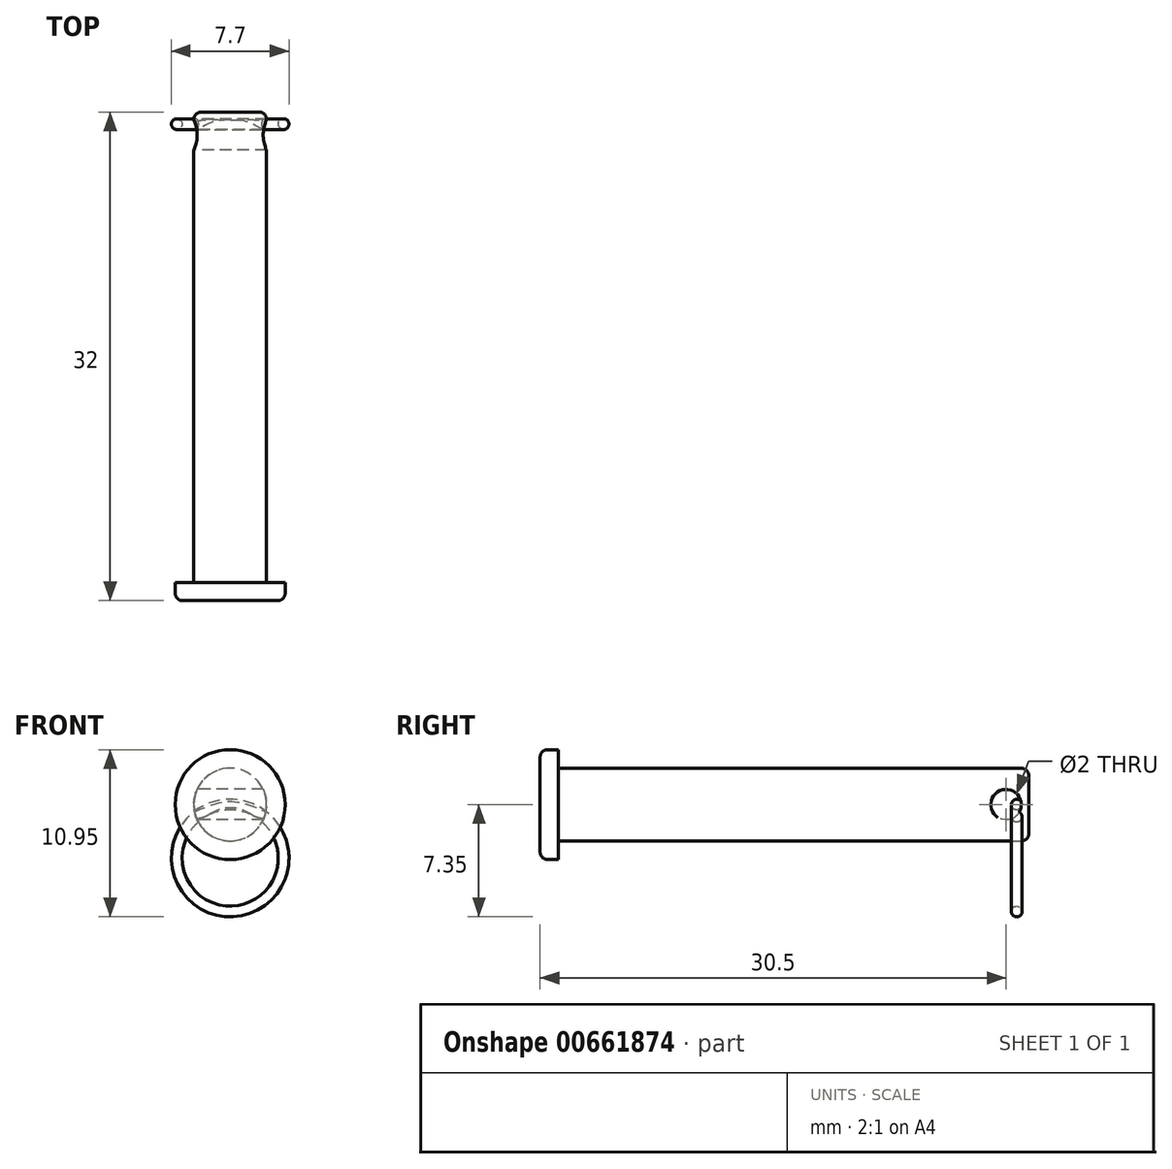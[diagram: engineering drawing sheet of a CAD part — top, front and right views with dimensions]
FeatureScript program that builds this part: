
annotation { "Feature Type Name" : "Feature", "Feature Type Description" : "" }
export const myFeature = defineFeature(function(context is Context, id is Id, definition is map)
    precondition{}
    {
        {
            var Q0;
            Q0=qCreatedBy(makeId("Right.planeOp"),FACE);
            var sketch = newSketch(context, id + "F0", { "sketchPlane" : qUnion([Q0])});
            skLineSegment(sketch, "E0", {"start": v(0, 0) * mm, "end": v(14.95, 0) * mm, "construction": true});
            skLineSegment(sketch, "E1", {"start": v(-1.2, 0) * mm, "end": v(-1.2, 3.6) * mm});
            skLineSegment(sketch, "E2", {"start": v(-1.2, 3.6) * mm, "end": v(0, 3.6) * mm});
            skLineSegment(sketch, "E3", {"start": v(0, 3.6) * mm, "end": v(0, 2.38) * mm});
            skLineSegment(sketch, "E4", {"start": v(0, 2.38) * mm, "end": v(30.8, 2.38) * mm});
            skLineSegment(sketch, "E5", {"start": v(30.8, 2.38) * mm, "end": v(30.8, 0) * mm});
            skLineSegment(sketch, "E6", {"start": v(30.8, 0) * mm, "end": v(-1.2, 0) * mm});
            skLineSegment(sketch, "E7", {"start": v(30, 0) * mm, "end": v(30, 2.38) * mm, "construction": true});
            skPoint(sketch, "E8.centerSnap0", {"position": v(30, 1.2) * mm});
            skSolve(sketch);
        }
        {
            var Q0;
            Q0 = qSketchRegion(id + "F0", true);
            var Q1;
            Q1=sQuery(id+"F0.wireOp",EDGE,"E6");
            revolve(context, id + "F1", {"surfaceOperationType" : NewSurfaceOperationType.NEW, "entities" : qUnion([Q0]), "axis" : qUnion([Q1]), "revolveType" : RevolveType.FULL});
        }
        {
            var Q0;
            Q0=qCreatedBy(makeId("Right.planeOp"),FACE);
            var sketch = newSketch(context, id + "F2", { "sketchPlane" : qUnion([Q0])});
            skCircle(sketch, "E9", {"center": v(29.3, 0) * mm, "radius": 1 * mm});
            skSolve(sketch);
        }
        {
            var Q0;
            Q0 = qSketchRegion(id + "F2", true);
            extrude(context, id + "F3", {"entities" : qUnion([Q0]), "operationType" : NewBodyOperationType.REMOVE, "depth" : 25 * mm, "offsetDistance" : 25 * mm, "symmetric" : true});
        }
        {
            var Q0;
            Q0=makeQuery(id+"F1.opRevolve","SWEPT_EDGE",EDGE,{"disambiguationData":[OSD([sQuery(id+"F0.wireOp",EDGE,"E1"),sQuery(id+"F0.wireOp",EDGE,"E2")])]});
            var Q1;
            Q1=makeQuery(id+"F1.opRevolve","SWEPT_EDGE",EDGE,{"disambiguationData":[OSD([sQuery(id+"F0.wireOp",EDGE,"E4"),sQuery(id+"F0.wireOp",EDGE,"E5")])]});
            fillet(context, id + "F4", {"entities" : qUnion([Q0, Q1]), "radius" : 0.5 * mm, "tangentPropagation" : true, "allowEdgeOverflow" : false});
        }
        {
            var Q0;
            Q0=qCreatedBy(makeId("Right.planeOp"),FACE);
            var sketch = newSketch(context, id + "F5", { "sketchPlane" : qUnion([Q0])});
            skCircle(sketch, "E10", {"center": v(30, 0) * mm, "radius": 0.35 * mm});
            skLineSegment(sketch, "E11", {"start": v(25.23, -3.5) * mm, "end": v(31.4, -3.5) * mm, "construction": true});
            skSolve(sketch);
        }
        {
            var Q0;
            Q0 = qSketchRegion(id + "F5", true);
            var Q1;
            Q1=sQuery(id+"F5.wireOp",EDGE,"E11");
            revolve(context, id + "F6", {"operationType" : NewBodyOperationType.ADD, "surfaceOperationType" : NewSurfaceOperationType.NEW, "entities" : qUnion([Q0]), "axis" : qUnion([Q1]), "revolveType" : RevolveType.FULL});
        }
    });
